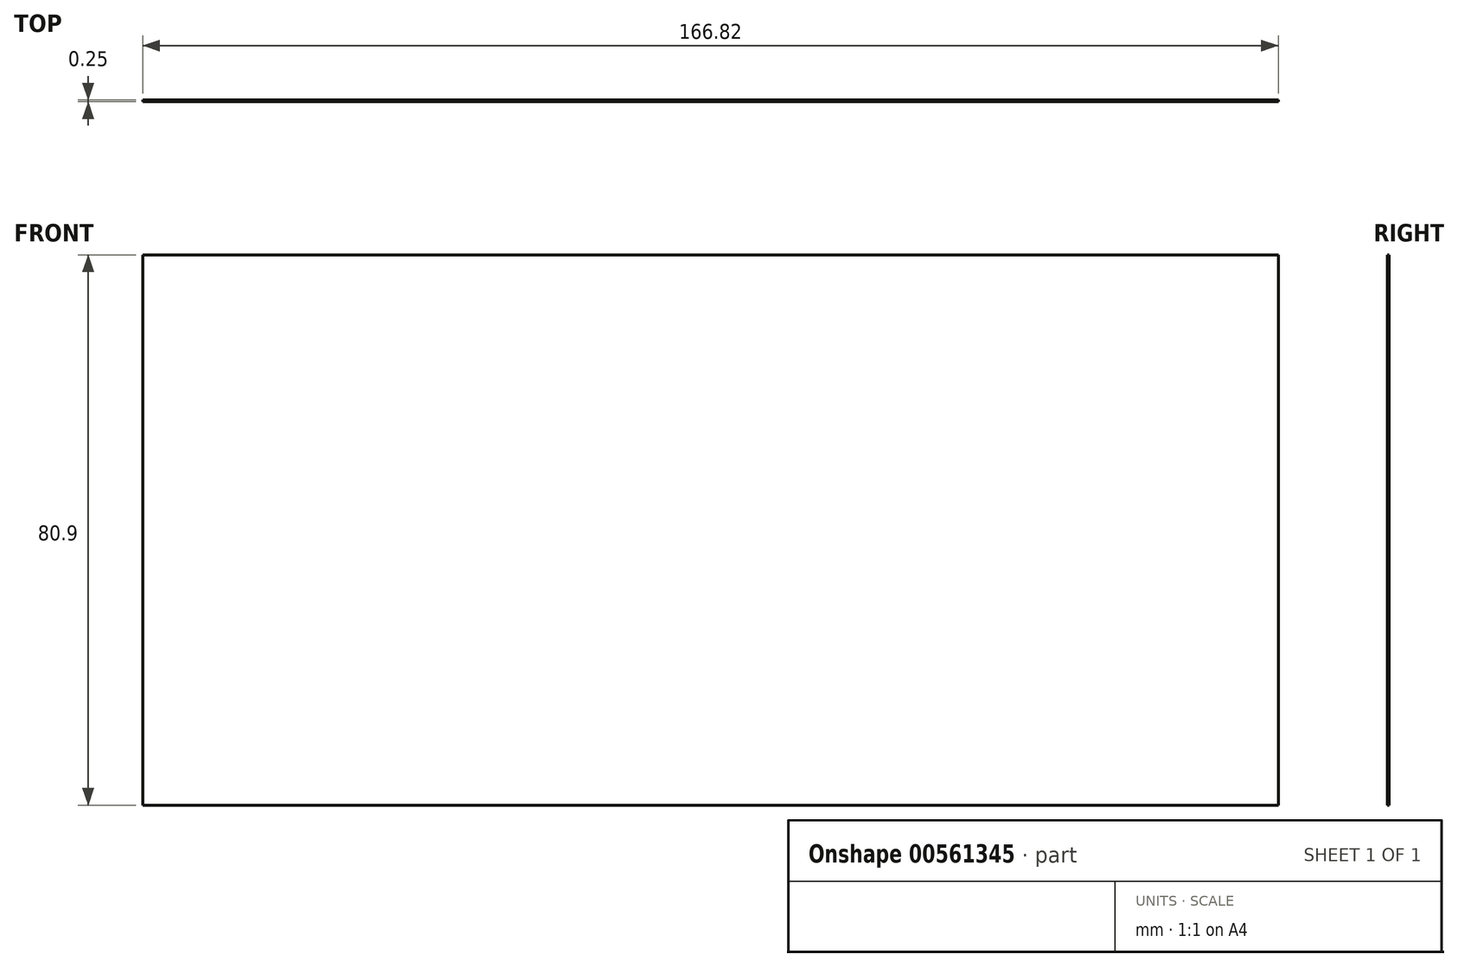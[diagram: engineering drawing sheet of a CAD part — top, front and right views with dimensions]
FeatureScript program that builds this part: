
annotation { "Feature Type Name" : "Feature", "Feature Type Description" : "" }
export const myFeature = defineFeature(function(context is Context, id is Id, definition is map)
    precondition{}
    {
        {
            var Q0;
            Q0=qCreatedBy(makeId("Front.planeOp"),FACE);
            var sketch = newSketch(context, id + "F0", { "sketchPlane" : qUnion([Q0])});
            skLineSegment(sketch, "E0.bottom", {"start": v(82.25, -41.04) * mm, "end": v(-84.57, -41.04) * mm});
            skLineSegment(sketch, "E0.top", {"start": v(82.25, 39.86) * mm, "end": v(-84.57, 39.86) * mm});
            skLineSegment(sketch, "E0.left", {"start": v(82.25, -41.04) * mm, "end": v(82.25, 39.86) * mm});
            skLineSegment(sketch, "E0.right", {"start": v(-84.57, -41.04) * mm, "end": v(-84.57, 39.86) * mm});
            skSolve(sketch);
        }
        {
            var Q0;
            Q0=makeQuery(id+"F0.imprint","IMPRINT",FACE,{"disambiguationData":[TD([[makeQuery(id+"F0.imprint","IMPRINT",EDGE,{"derivedFrom":sQuery(id+"F0.wireOp",EDGE,"E0.bottom")}),-1.0]])]});
            extrude(context, id + "F1", {"entities" : qUnion([Q0]), "depth" : 0.25 * mm, "offsetDistance" : 25.4 * mm});
        }
    });
